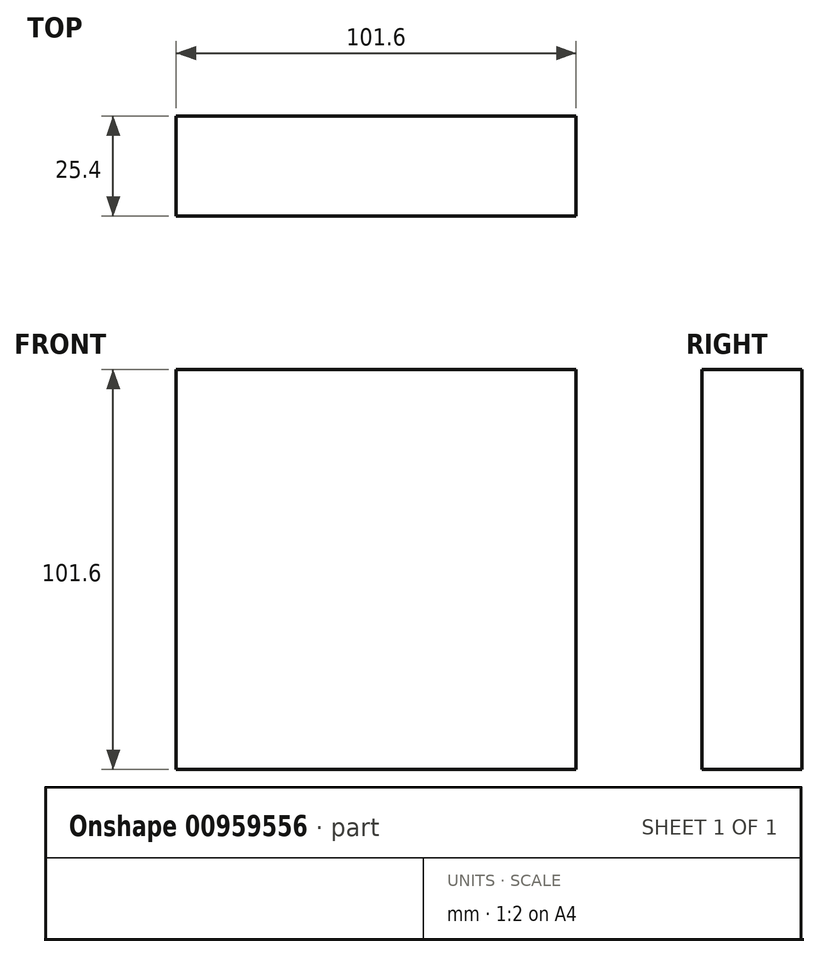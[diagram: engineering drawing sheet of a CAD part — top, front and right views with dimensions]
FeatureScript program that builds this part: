
annotation { "Feature Type Name" : "Feature", "Feature Type Description" : "" }
export const myFeature = defineFeature(function(context is Context, id is Id, definition is map)
    precondition{}
    {
        {
            var Q0;
            Q0=qCreatedBy(makeId("Front.planeOp"),FACE);
            var sketch = newSketch(context, id + "F0", { "sketchPlane" : qUnion([Q0])});
            skLineSegment(sketch, "E0.bottom", {"start": v(-45.52, 50.8) * mm, "end": v(56.08, 50.8) * mm});
            skLineSegment(sketch, "E0.top", {"start": v(-45.52, -50.8) * mm, "end": v(56.08, -50.8) * mm});
            skLineSegment(sketch, "E0.left", {"start": v(-45.52, 50.8) * mm, "end": v(-45.52, -50.8) * mm});
            skLineSegment(sketch, "E0.right", {"start": v(56.08, 50.8) * mm, "end": v(56.08, -50.8) * mm});
            skPoint(sketch, "E0.middle", {"position": v(5.28, 0) * mm});
            skSolve(sketch);
        }
        {
            var Q0;
            Q0=makeQuery(id+"F0.imprint","IMPRINT",FACE,{"disambiguationData":[TD([[makeQuery(id+"F0.imprint","IMPRINT",EDGE,{"derivedFrom":sQuery(id+"F0.wireOp",EDGE,"E0.bottom")}),-1.0]])]});
            extrude(context, id + "F1", {"entities" : qUnion([Q0]), "depth" : 25.4 * mm, "offsetDistance" : 25.4 * mm});
        }
    });
